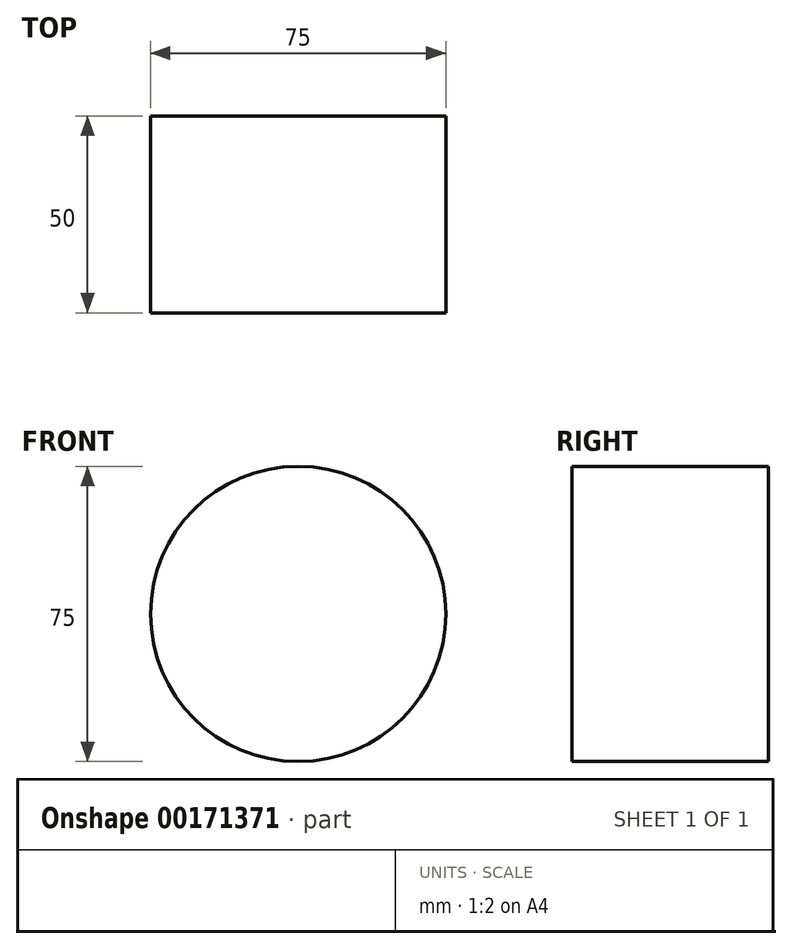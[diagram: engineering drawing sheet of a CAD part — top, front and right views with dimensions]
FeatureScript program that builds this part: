
annotation { "Feature Type Name" : "Feature", "Feature Type Description" : "" }
export const myFeature = defineFeature(function(context is Context, id is Id, definition is map)
    precondition{}
    {
        {
            var Q0;
            Q0=qCreatedBy(makeId("Front.planeOp"),FACE);
            var sketch = newSketch(context, id + "F0", { "sketchPlane" : qUnion([Q0])});
            skCircle(sketch, "E0", {"center": v(0, 0) * mm, "radius": 37.5 * mm});
            skSolve(sketch);
        }
        {
            var Q0;
            Q0=makeQuery(id+"F0.imprint","IMPRINT",FACE,{"disambiguationData":[TD([[makeQuery(id+"F0.imprint","IMPRINT",EDGE,{"derivedFrom":sQuery(id+"F0.wireOp",EDGE,"E0")}),1.0]])]});
            extrude(context, id + "F1", {"entities" : qUnion([Q0]), "depth" : 50 * mm});
        }
    });
